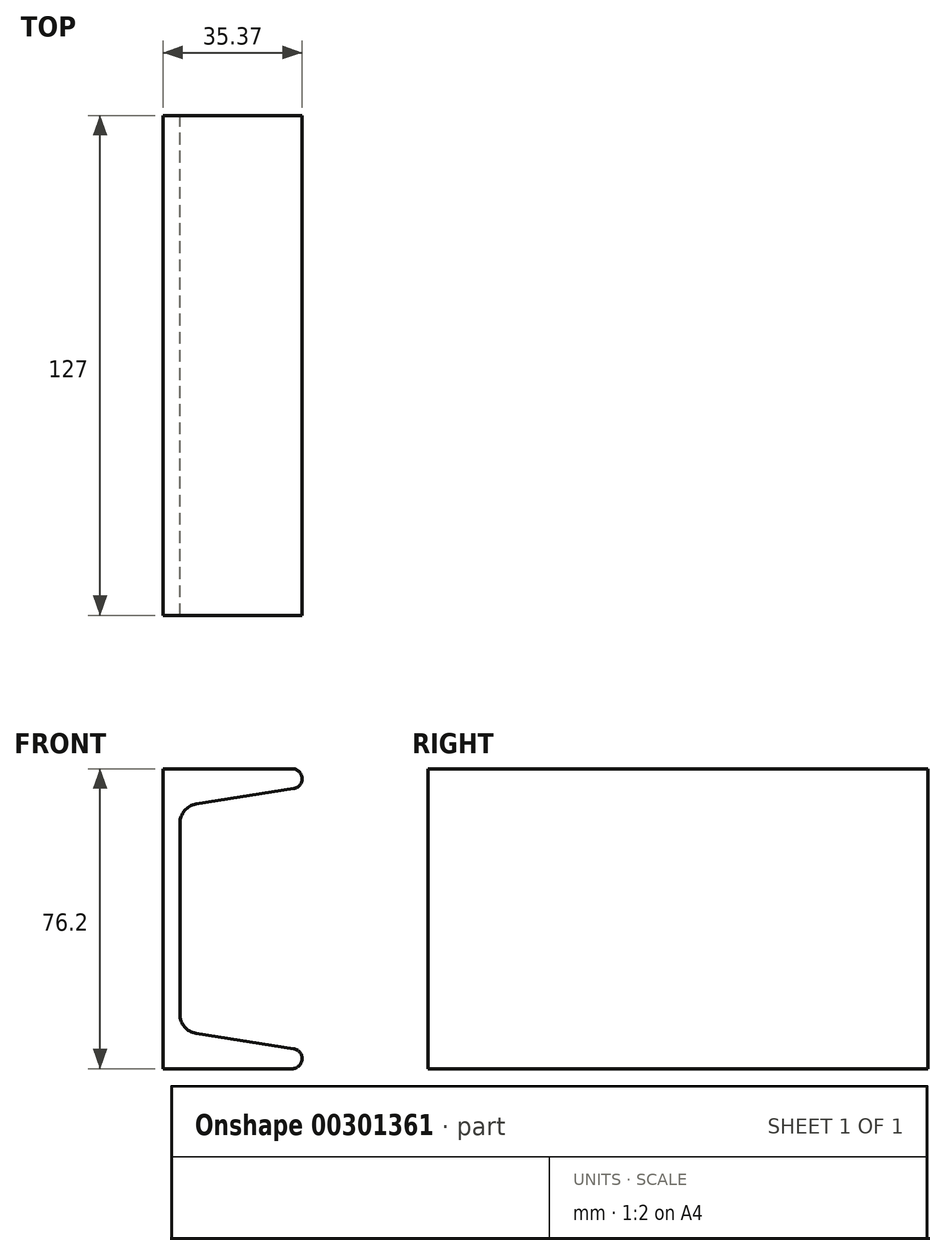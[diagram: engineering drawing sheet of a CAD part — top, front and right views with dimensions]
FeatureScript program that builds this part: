
annotation { "Feature Type Name" : "Feature", "Feature Type Description" : "" }
export const myFeature = defineFeature(function(context is Context, id is Id, definition is map)
    precondition{}
    {
        {
            var Q0;
            Q0=qCreatedBy(makeId("Front.planeOp"),FACE);
            var sketch = newSketch(context, id + "F0", { "sketchPlane" : qUnion([Q0])});
            skLineSegment(sketch, "E0", {"start": v(0, 0) * mm, "end": v(0, 76.2) * mm});
            skLineSegment(sketch, "E1", {"start": v(0, 76.2) * mm, "end": v(32.83, 76.2) * mm});
            skLineSegment(sketch, "E2", {"start": v(33.22, 71.15) * mm, "end": v(8.41, 67.22) * mm});
            skLineSegment(sketch, "E3", {"start": v(4.32, 62.43) * mm, "end": v(4.32, 13.77) * mm});
            skLineSegment(sketch, "E4", {"start": v(8.41, 8.98) * mm, "end": v(33.22, 5.05) * mm});
            skLineSegment(sketch, "E5", {"start": v(32.83, 0) * mm, "end": v(0, 0) * mm});
            skPoint(sketch, "E6.visualSharp", {"position": v(4.32, 9.63) * mm});
            skArc(sketch, "E6.filletArc", {"start": v(4.32, 13.77) * mm, "mid": v(5.48, 10.62) * mm, "end": v(8.41, 8.98) * mm});
            skPoint(sketch, "E7.visualSharp", {"position": v(4.32, 66.57) * mm});
            skArc(sketch, "E7.filletArc", {"start": v(8.41, 67.22) * mm, "mid": v(5.48, 65.58) * mm, "end": v(4.32, 62.43) * mm});
            skPoint(sketch, "E8.visualSharp", {"position": v(65.1, 76.2) * mm});
            skArc(sketch, "E8.filletArc", {"start": v(33.22, 71.15) * mm, "mid": v(35.36, 73.86) * mm, "end": v(32.83, 76.2) * mm});
            skPoint(sketch, "E9.visualSharp", {"position": v(65.1, 0) * mm});
            skArc(sketch, "E9.filletArc", {"start": v(32.83, 0) * mm, "mid": v(35.36, 2.34) * mm, "end": v(33.22, 5.05) * mm});
            skSolve(sketch);
        }
        {
            var Q0;
            Q0 = qSketchRegion(id + "F0", true);
            extrude(context, id + "F1", {"entities" : qUnion([Q0]), "depth" : 127 * mm});
        }
    });
